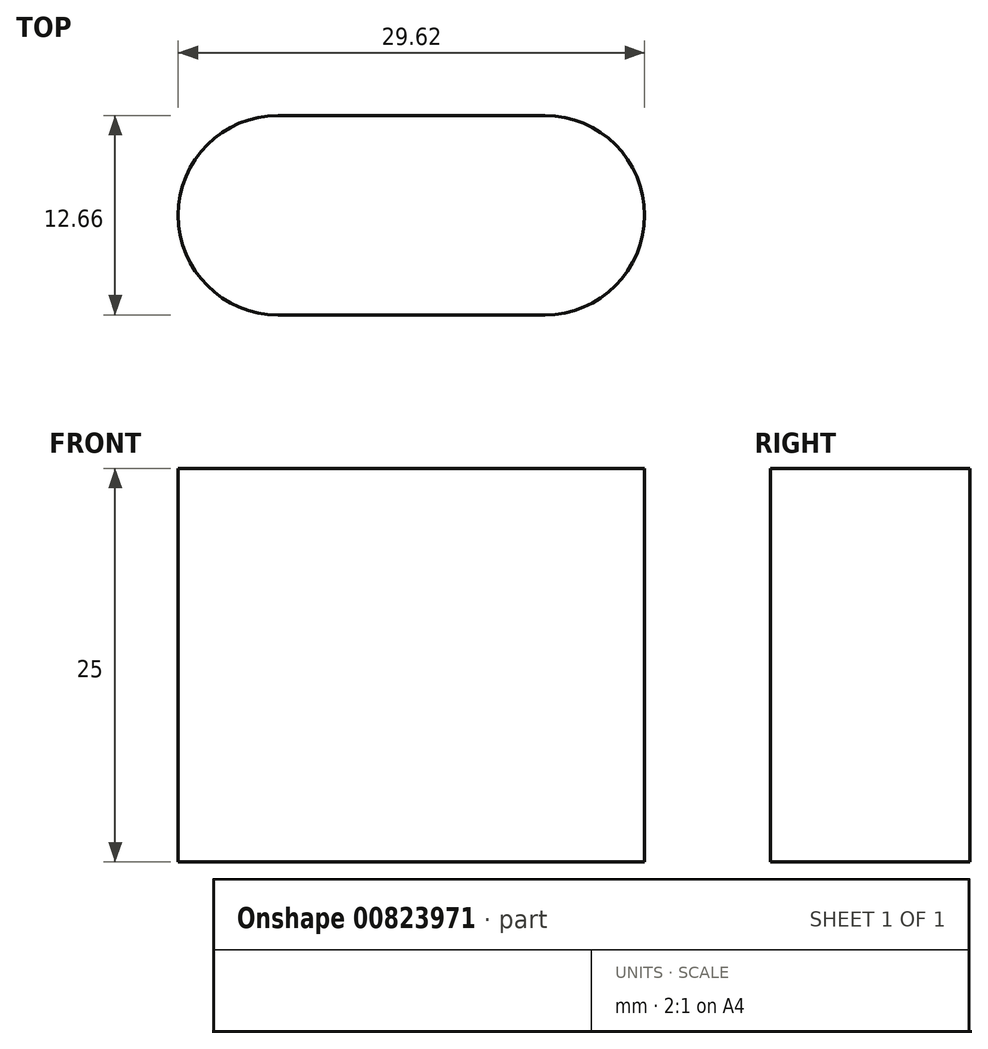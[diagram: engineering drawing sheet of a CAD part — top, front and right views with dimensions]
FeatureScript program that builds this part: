
annotation { "Feature Type Name" : "Feature", "Feature Type Description" : "" }
export const myFeature = defineFeature(function(context is Context, id is Id, definition is map)
    precondition{}
    {
        {
            var Q0;
            Q0=qCreatedBy(makeId("Top.planeOp"),FACE);
            var sketch = newSketch(context, id + "F0", { "sketchPlane" : qUnion([Q0])});
            skLineSegment(sketch, "E0.bottom", {"start": v(8.48, -6.33) * mm, "end": v(-8.48, -6.33) * mm});
            skLineSegment(sketch, "E0.top", {"start": v(8.48, 6.33) * mm, "end": v(-8.48, 6.33) * mm});
            skLineSegment(sketch, "E0.left", {"start": v(8.48, -6.33) * mm, "end": v(8.48, 6.33) * mm});
            skLineSegment(sketch, "E0.right", {"start": v(-8.48, -6.33) * mm, "end": v(-8.48, 6.33) * mm});
            skPoint(sketch, "E0.middle", {"position": v(0, 0) * mm});
            skCircle(sketch, "E1", {"center": v(-8.48, 0) * mm, "radius": 6.33 * mm});
            skCircle(sketch, "E2", {"center": v(8.48, 0) * mm, "radius": 6.33 * mm});
            skSolve(sketch);
        }
        {
            var Q0;
            Q0=qSketchRegion(id+"F0",true);
            extrude(context, id + "F1", {"entities" : qUnion([Q0]), "depth" : 2 * mm, "offsetDistance" : 25 * mm});
        }
        {
            var Q0;
            Q0=qSketchRegion(id+"F0",true);
            extrude(context, id + "F2", {"entities" : qUnion([Q0]), "operationType" : NewBodyOperationType.ADD, "depth" : 25 * mm, "offsetDistance" : 25 * mm});
        }
    });
